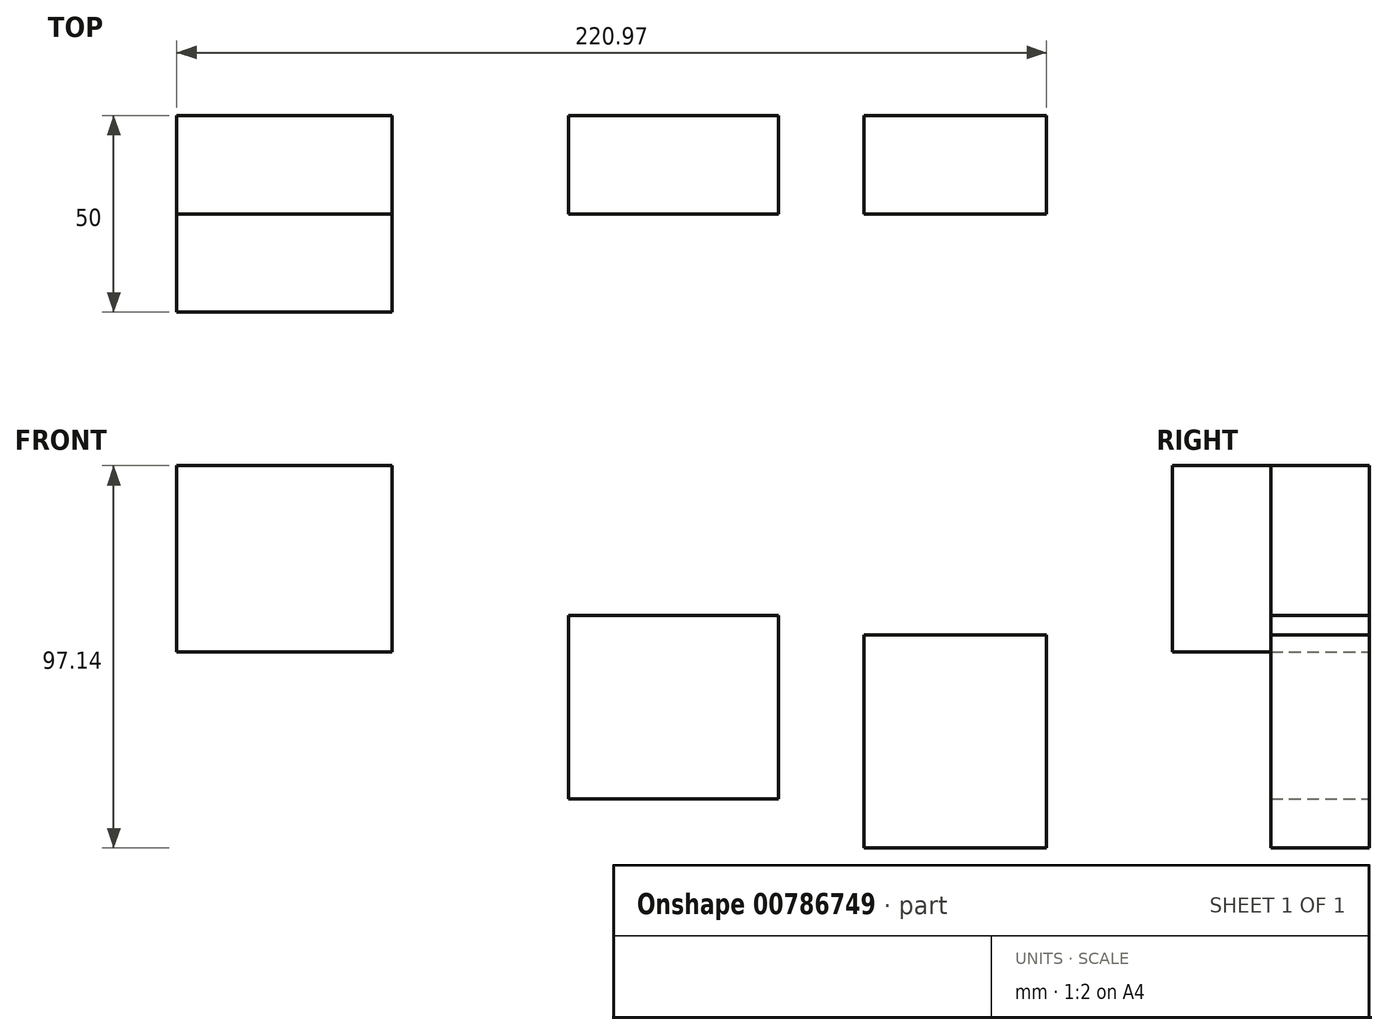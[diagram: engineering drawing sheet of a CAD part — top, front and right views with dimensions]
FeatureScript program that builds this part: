
annotation { "Feature Type Name" : "Feature", "Feature Type Description" : "" }
export const myFeature = defineFeature(function(context is Context, id is Id, definition is map)
    precondition{}
    {
        {
            var Q0;
            Q0=qCreatedBy(makeId("Front.planeOp"),FACE);
            var sketch = newSketch(context, id + "F0", { "sketchPlane" : qUnion([Q0])});
            skLineSegment(sketch, "E0.bottom", {"start": v(-158.38, 53.58) * mm, "end": v(-103.64, 53.58) * mm});
            skLineSegment(sketch, "E0.top", {"start": v(-158.38, 6.3) * mm, "end": v(-103.64, 6.3) * mm});
            skLineSegment(sketch, "E0.left", {"start": v(-158.38, 53.58) * mm, "end": v(-158.38, 6.3) * mm});
            skLineSegment(sketch, "E0.right", {"start": v(-103.64, 53.58) * mm, "end": v(-103.64, 6.3) * mm});
            skLineSegment(sketch, "E1.bottom", {"start": v(-58.91, 15.54) * mm, "end": v(-5.5, 15.54) * mm});
            skLineSegment(sketch, "E1.top", {"start": v(-58.91, -31.13) * mm, "end": v(-5.5, -31.13) * mm});
            skLineSegment(sketch, "E1.left", {"start": v(-58.91, 15.54) * mm, "end": v(-58.91, -31.13) * mm});
            skLineSegment(sketch, "E1.right", {"start": v(-5.5, 15.54) * mm, "end": v(-5.5, -31.13) * mm});
            skLineSegment(sketch, "E2.bottom", {"start": v(62.59, 10.56) * mm, "end": v(16.19, 10.56) * mm});
            skLineSegment(sketch, "E2.top", {"start": v(62.59, -43.56) * mm, "end": v(16.19, -43.56) * mm});
            skLineSegment(sketch, "E2.left", {"start": v(62.59, 10.56) * mm, "end": v(62.59, -43.56) * mm});
            skLineSegment(sketch, "E2.right", {"start": v(16.19, 10.56) * mm, "end": v(16.19, -43.56) * mm});
            skSolve(sketch);
        }
        {
            var Q0;
            Q0 = qSketchRegion(id + "F0", true);
            extrude(context, id + "F1", {"entities" : qUnion([Q0]), "depth" : 25 * mm, "offsetDistance" : 25 * mm});
        }
        {
            var Q0;
            Q0=makeQuery(id+"F1.opExtrude","CAP_FACE",FACE,{"disambiguationData":[OSD([sQuery(id+"F0.wireOp",EDGE,"E0.bottom"),sQuery(id+"F0.wireOp",EDGE,"E0.top"),sQuery(id+"F0.wireOp",EDGE,"E0.left"),sQuery(id+"F0.wireOp",EDGE,"E0.right")])],"isStart":false});
            extrude(context, id + "F2", {"entities" : qUnion([Q0]), "depth" : 25 * mm, "offsetDistance" : 25 * mm});
        }
    });
